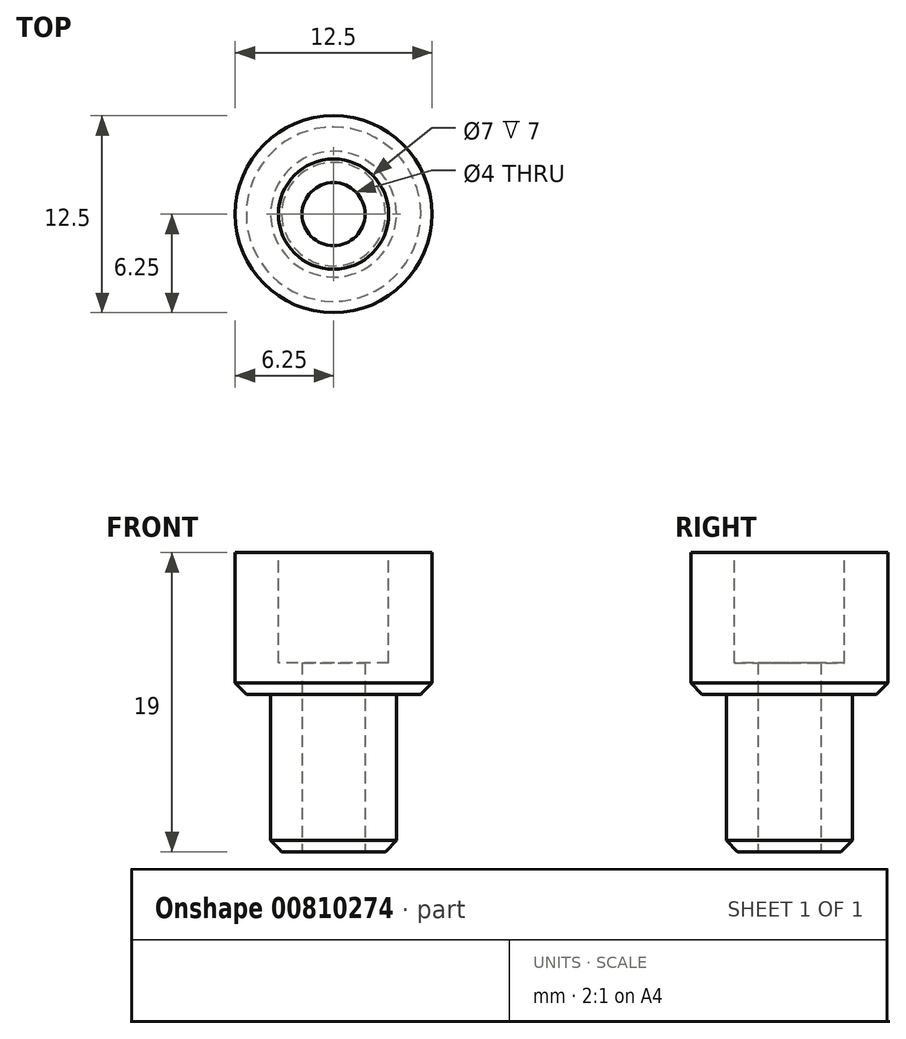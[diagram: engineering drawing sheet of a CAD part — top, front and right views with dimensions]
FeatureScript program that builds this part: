
annotation { "Feature Type Name" : "Feature", "Feature Type Description" : "" }
export const myFeature = defineFeature(function(context is Context, id is Id, definition is map)
    precondition{}
    {
        {
            var Q0;
            Q0=qCreatedBy(makeId("Top.planeOp"),FACE);
            var sketch = newSketch(context, id + "F0", { "sketchPlane" : qUnion([Q0])});
            skCircle(sketch, "E0", {"center": v(0, 0) * mm, "radius": 6.25 * mm});
            skSolve(sketch);
        }
        {
            var Q0;
            Q0 = qSketchRegion(id + "F0", true);
            extrude(context, id + "F1", {"entities" : qUnion([Q0]), "depth" : 9 * mm, "offsetDistance" : 25 * mm});
        }
        {
            var Q0;
            Q0=makeQuery(id+"F1.opExtrude","CAP_FACE",FACE,{"disambiguationData":[OSD([sQuery(id+"F0.wireOp",EDGE,"E0")])],"isStart":false});
            var sketch = newSketch(context, id + "F2", { "sketchPlane" : qUnion([Q0])});
            skCircle(sketch, "E1", {"center": v(0, 0) * mm, "radius": 3.5 * mm});
            skSolve(sketch);
        }
        {
            var Q0;
            Q0 = qSketchRegion(id + "F2", true);
            extrude(context, id + "F3", {"entities" : qUnion([Q0]), "operationType" : NewBodyOperationType.REMOVE, "oppositeDirection" : true, "depth" : 7 * mm, "offsetDistance" : 25 * mm});
        }
        {
            var Q0;
            Q0=makeQuery(id+"F1.opExtrude","CAP_FACE",FACE,{"disambiguationData":[OSD([sQuery(id+"F0.wireOp",EDGE,"E0")])],"isStart":true});
            var sketch = newSketch(context, id + "F4", { "sketchPlane" : qUnion([Q0])});
            skCircle(sketch, "E2", {"center": v(0, 0) * mm, "radius": 4 * mm});
            skSolve(sketch);
        }
        {
            var Q0;
            Q0 = qSketchRegion(id + "F4", true);
            extrude(context, id + "F5", {"entities" : qUnion([Q0]), "operationType" : NewBodyOperationType.ADD, "depth" : 10 * mm, "offsetDistance" : 25 * mm});
        }
        {
            var Q0;
            Q0=makeQuery(id+"F5.opExtrude","CAP_FACE",FACE,{"disambiguationData":[OSD([sQuery(id+"F4.wireOp",EDGE,"E2")])],"isStart":false});
            var sketch = newSketch(context, id + "F6", { "sketchPlane" : qUnion([Q0])});
            skCircle(sketch, "E3", {"center": v(0, 0) * mm, "radius": 2 * mm});
            skSolve(sketch);
        }
        {
            var Q0;
            Q0 = qSketchRegion(id + "F6", true);
            extrude(context, id + "F7", {"entities" : qUnion([Q0]), "operationType" : NewBodyOperationType.REMOVE, "oppositeDirection" : true, "depth" : 12 * mm, "offsetDistance" : 25 * mm});
        }
        {
            var Q0;
            Q0=makeQuery(id+"F1.opExtrude","CAP_EDGE",EDGE,{"disambiguationData":[OSD([sQuery(id+"F0.wireOp",EDGE,"E0")])],"isStart":true});
            chamfer(context, id + "F8", {"entities" : qUnion([Q0]), "chamferType" : ChamferType.OFFSET_ANGLE, "width" : 0.71 * mm, "oppositeDirection" : false, "angle" : 45 * degree, "tangentPropagation" : true});
        }
        {
            var Q0;
            Q0=makeQuery(id+"F5.opExtrude","CAP_EDGE",EDGE,{"disambiguationData":[OSD([sQuery(id+"F4.wireOp",EDGE,"E2")])],"isStart":false});
            chamfer(context, id + "F9", {"entities" : qUnion([Q0]), "chamferType" : ChamferType.OFFSET_ANGLE, "width" : 0.71 * mm, "oppositeDirection" : false, "angle" : 45 * degree, "tangentPropagation" : true});
        }
    });
